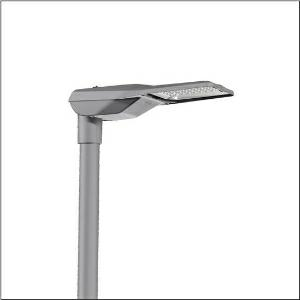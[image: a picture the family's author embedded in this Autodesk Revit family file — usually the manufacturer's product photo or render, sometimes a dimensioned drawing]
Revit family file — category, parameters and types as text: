
# Revit family: streetlight_sl_21_iq_mini___p0_8a_5xe2u31v08jb_63ec
name_source: partatom
category: Lighting Fixtures
units: mm (PartAtom-declared; Revit-internal decimal feet)

## family parameters
Cut with Voids When Loaded = No
Host = Face
Light Source = No
Part Type = Normal
Room Calculation Point = No
Round Connector Dimension = Use Diameter
Shared = No

## types (1)
- --- (1 x LED, 11310 lm, 72.5 W, 3000K)
    Apparent Load = 73 VA
    CIE Flux Codes = 36 69 97 100 100
    Color Rendering = 70
    Color Temperature = 3000K
    Default Elevation = 1800 mm
    Description = Streetlight SL 21 iQ mini, mast luminaire, primary light control with lens, of PMMA, primary optical cover: cover, of toughened safety glass, transparent, light distribution: P0.8a, light emission: direct distribution, primary light characteristic: asymmetric, installation type: post-top, side-entry, LED, High Power LED, rated luminous flux: 11.310lm, luminous efficacy: 156lm/W, light colour: 730, colour temperature: 3000K, control gear: iQ-Street Remote, D4i with power reduction, control: pre-setting: logarithmic dimming characteristic, Street-Remote, Auto-Match, Temp-Guard, Lumen-Switch, Night-Set, Smart-Wire, Light-Fading, Desk-Remote (wireless, voltage-free reading and setting of iQ features in the workshop via application-optimized NFC function/RFID function), optimised constant luminous flux control (CLO 2.0), mains connection: 220..240V, AC, 50/60Hz, start of lifetime: 73W, end of service life: 76W, reduction: 33W, luminaire housing, of diecast aluminium, powder-coated, Siteco® metallic grey (DB 702S), corrosivity category C5 mid according to DIN EN ISO 12944, please order mast flange separately, inclination adjustable: 0°, 5°, 10°, 15°, sealing non-destructively replaceable, multi-level sealing system, length: 628mm, width: 235mm, height: 110mm, mast flange for spigot size: 42mm (side-entry): 5XC10008XM4, 60/48mm (side-entry/post-top): 5XC10108XM2, 76/60mm (side-entry/post-top): 5XC10108XM1, mounting height: 4..8m, Smart Interface above, protection rating (complete): IP66, insulation class (complete): insulation class II (safety insulation), certification: CE, ENEC, ENEC+, VDE, impact resistance: IK10, permissible operating ambient temperature for outdoor applications: -40..+50°C, standard-compliant lighting for roads and squares, packaging unit: 1 piece

Light Distribution: P0.8a
    Height = 110 mm
    Lamp = 1 x LED
    Lamp Light Flux = 11310 lm
    Lamp Power = 72.5 W
    Lamp count = 1
    Length = 625 mm
    Luminous efficacy = 156 lm/W
    Manufacturer = Siteco
    ModVariant = No
    Model = 5XE2U31V08JB
    Number of Poles = 1
    OnlyDefault = Yes
    Power Factor = 1
    Product Name = Streetlight SL 21 iQ mini | P0.8a
    Product group = mast luminaire | pylon top
    ProductGroupID = 6100
    Protection Class = Protection class II
    Protection Degree = IP 66
    RLX_Detail_Level = 1
    RLX_Emergency_Light_Flux = 0 lm
    RLX_Emergency_Type = 0
    RLX_Emergency_Type_DB = No
    RlxData = <blob elided: 26289 chars, md5=1626e4d1>
    Socket = socket
    Standby Power = 0 W
    System Light Flux = 11310 lm
    System Power = 73 W
    Type Comments = factory setting: luminous flux: 100 % | dim-lin: 254 | 755 mA
    Type Image = l_1003515.jpg
    URL = http://relux.com
    VarID = @adj_072136
    Voltage = 0 V
    Weight = 0.00 kg
    Width = 234 mm

## geometry (parser evidence)
native form markers: Blend x4, Sweep x13
no freeform markers — native parametric forms only
